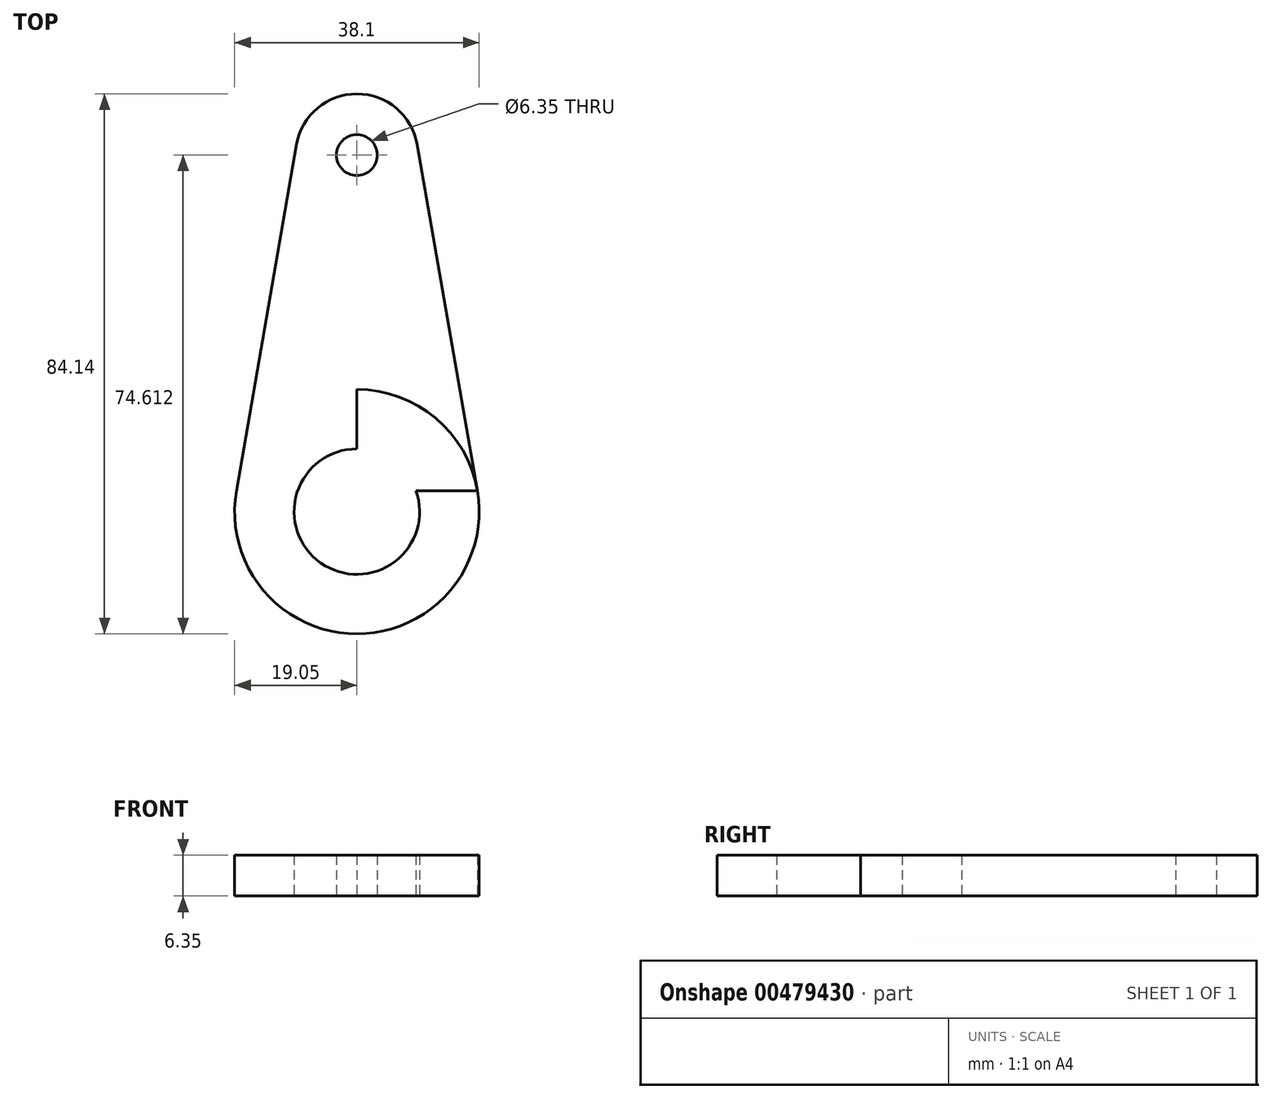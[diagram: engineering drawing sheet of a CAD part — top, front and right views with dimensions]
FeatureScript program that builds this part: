
annotation { "Feature Type Name" : "Feature", "Feature Type Description" : "" }
export const myFeature = defineFeature(function(context is Context, id is Id, definition is map)
    precondition{}
    {
        {
            var Q0;
            Q0=qCreatedBy(makeId("Top.planeOp"),FACE);
            var sketch = newSketch(context, id + "F0", { "sketchPlane" : qUnion([Q0]), "disableImprinting" : false});
            skCircle(sketch, "E0", {"center": v(0, 0) * mm, "radius": 19.05 * mm});
            skCircle(sketch, "E1", {"center": v(0, 0) * mm, "radius": 9.78 * mm});
            skCircle(sketch, "E2", {"center": v(0, 55.56) * mm, "radius": 9.53 * mm});
            skCircle(sketch, "E3", {"center": v(0, 55.56) * mm, "radius": 3.18 * mm});
            skLineSegment(sketch, "E4", {"start": v(0, 55.56) * mm, "end": v(0, 0) * mm});
            skLineSegment(sketch, "E5", {"start": v(-9.39, 57.19) * mm, "end": v(9.39, 57.19) * mm});
            skLineSegment(sketch, "E6", {"start": v(9.39, 57.19) * mm, "end": v(18.77, 3.25) * mm});
            skLineSegment(sketch, "E7", {"start": v(18.77, 3.25) * mm, "end": v(-18.77, 3.25) * mm});
            skLineSegment(sketch, "E8", {"start": v(-18.77, 3.25) * mm, "end": v(-9.39, 57.19) * mm});
            skSolve(sketch);
        }
        {
            var Q0;
            {var subQ0=sQuery(id+"F0.wireOp",EDGE,"E6");Q0=makeQuery(id+"F0.imprint","IMPRINT",FACE,{"disambiguationData":[TD([[makeQuery(id+"F0.imprint","IMPRINT",EDGE,{"derivedFrom":subQ0}),-1.0]])]});}
            var Q1;
            {var subQ0=sQuery(id+"F0.wireOp",EDGE,"E8");Q1=makeQuery(id+"F0.imprint","IMPRINT",FACE,{"disambiguationData":[TD([[makeQuery(id+"F0.imprint","IMPRINT",EDGE,{"derivedFrom":subQ0}),-1.0]])]});}
            var Q2;
            {var subQ3=sQuery(id+"F0.wireOp",EDGE,"E4");var subQ5=sQuery(id+"F0.wireOp",EDGE,"E3");var subQ6=makeQuery(id+"F0.imprint","INTERSECT",VERTEX,{"derivedFrom":[subQ5,subQ3]});Q2=makeQuery(id+"F0.imprint","IMPRINT",FACE,{"disambiguationData":[TD([[makeQuery(id+"F0.imprint","IMPRINT",EDGE,{"disambiguationData":[TD([[subQ6,1.0]])],"derivedFrom":subQ5}),-1.0]])]});}
            var Q3;
            {var subQ3=sQuery(id+"F0.wireOp",EDGE,"E4");var subQ5=sQuery(id+"F0.wireOp",EDGE,"E3");var subQ7=makeQuery(id+"F0.imprint","INTERSECT",VERTEX,{"derivedFrom":[subQ5,subQ3]});Q3=makeQuery(id+"F0.imprint","IMPRINT",FACE,{"disambiguationData":[TD([[makeQuery(id+"F0.imprint","IMPRINT",EDGE,{"disambiguationData":[TD([[subQ7,-1.0]])],"derivedFrom":subQ5}),-1.0]])]});}
            var Q4;
            {var subQ0=sQuery(id+"F0.wireOp",EDGE,"E5");var subQ4=sQuery(id+"F0.wireOp",EDGE,"E3");var subQ5=makeQuery(id+"F0.imprint","INTERSECT",VERTEX,{"disambiguationData":[OD(0.0)],"derivedFrom":[subQ4,subQ0]});Q4=makeQuery(id+"F0.imprint","IMPRINT",FACE,{"disambiguationData":[TD([[makeQuery(id+"F0.imprint","IMPRINT",EDGE,{"disambiguationData":[TD([[subQ5,1.0]])],"derivedFrom":subQ4}),-1.0]])]});}
            var Q5;
            {var subQ1=sQuery(id+"F0.wireOp",EDGE,"E0");var subQ7=makeQuery(id+"F0.imprint","INTERSECT",VERTEX,{"derivedFrom":[subQ1,sQuery(id+"F0.wireOp",EDGE,"E6")]});Q5=makeQuery(id+"F0.imprint","IMPRINT",FACE,{"disambiguationData":[TD([[makeQuery(id+"F0.imprint","IMPRINT",EDGE,{"disambiguationData":[TD([[subQ7,1.0]])],"derivedFrom":subQ1}),1.0]])]});}
            var Q6;
            {var subQ1=sQuery(id+"F0.wireOp",EDGE,"E0");var subQ8=makeQuery(id+"F0.imprint","INTERSECT",VERTEX,{"derivedFrom":[subQ1,sQuery(id+"F0.wireOp",EDGE,"E8")]});Q6=makeQuery(id+"F0.imprint","IMPRINT",FACE,{"disambiguationData":[TD([[makeQuery(id+"F0.imprint","IMPRINT",EDGE,{"disambiguationData":[TD([[subQ8,1.0]])],"derivedFrom":subQ1}),1.0]])]});}
            var Q7;
            {var subQ0=sQuery(id+"F0.wireOp",EDGE,"E7");var subQ1=sQuery(id+"F0.wireOp",EDGE,"E0");var subQ2=makeQuery(id+"F0.imprint","INTERSECT",VERTEX,{"disambiguationData":[OD(0.0)],"derivedFrom":[subQ1,subQ0]});Q7=makeQuery(id+"F0.imprint","IMPRINT",FACE,{"disambiguationData":[TD([[makeQuery(id+"F0.imprint","IMPRINT",EDGE,{"disambiguationData":[TD([[subQ2,1.0]])],"derivedFrom":subQ1}),1.0]])]});}
            extrude(context, id + "F1", {"entities" : qUnion([Q0, Q1, Q2, Q3, Q4, Q5, Q6, Q7]), "depth" : 6.35 * mm, "offsetDistance" : 25.4 * mm});
        }
    });
